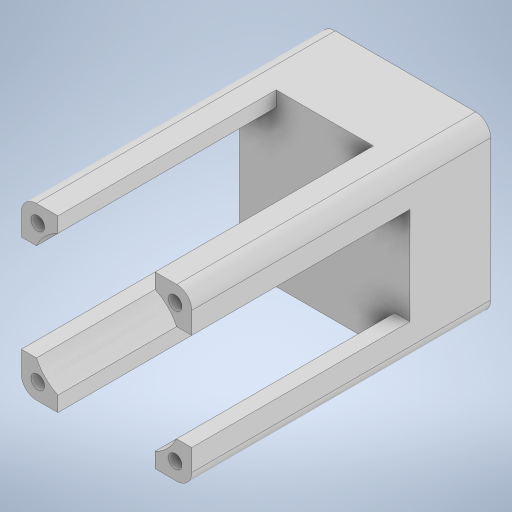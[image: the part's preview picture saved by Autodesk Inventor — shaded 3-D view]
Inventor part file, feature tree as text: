
AUTODESK INVENTOR PART (.ipt)
format: ipt  version: 2024 (Build 280153000, 153)  size: 329,216 bytes
history: native  units: in
note: dims shown in document units (in); Inventor stores cm internally (conversion verified against a paired STEP export)
features: extrude x6, sketch x6, fillet x2
ambient origin geometry x8: Origin, YZ Plane, XZ Plane, XY Plane, X Axis, Y Axis, Z Axis, Center Point
bodies: Solid1 (feature_tree)
feature tree (14):
  extrude  "Extrusion1"  Depth=4.4882in
  fillet  "Fillet1"  Radius=7.874in
  fillet  "Fillet2"  Radius=0.3937in
  extrude  "Extrusion3"  Depth=0.3937in
  extrude  "Extrusion5"  Depth=0.4346in
  extrude  "Extrusion6"  Depth=0.3543in
  extrude  "Extrusion8"  Depth=0.4346in
  extrude  "Extrusion9"  Depth=1.8898in
  sketch  "Sketch1"  dims[d0=4.4882in d1=4.4882in d2=7.874in d3=0.0in d9=0.3937in]
  sketch  "Sketch3"  dims[d10=0.3937in d11=0.3543in]
  sketch  "Sketch6"  dims[d12=0.4346in d13=0.4346in]
  sketch  "Sketch7"  dims[d14=0.3543in d15=0.3543in]
  sketch  "Sketch9"  dims[d16=0.3543in d17=0.4346in]
  sketch  "Sketch10"  dims[d18=0.4346in d19=0.4346in d20=0.4346in d21=0.4346in d22=0.4346in d23=19.685in d24=0.0in d30=0.5709in d31=0.3988in d32=0.5709in d33=0.3988in d34=1.1811in d35=0.5709in d36=0.3988in d37=0.5709in d38=0.3988in d39=1.1811in d40=0.5709in d41=0.3988in d42=0.5709in d44=1.1811in d45=0.3988in d46=0.5709in d47=0.3988in d48=0.5709in d49=0.3988in d50=1.1811in d51=5.748in d52=2.874in d53=0.0in d54=0.0in d58=4.3307in d59=0.1181in d60=0.0in d66=0.9449in d68=2.2441in d69=2.2441in d70=1.8898in d71=0.0in d72=0.5906in d73=0.315in d74=0.1575in d75=2.2441in d76=1.6535in d77=1.8898in d78=0.0in d28=0.0197in d29=0.0344in d61=0.0197in d62=0.0344in]
